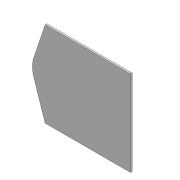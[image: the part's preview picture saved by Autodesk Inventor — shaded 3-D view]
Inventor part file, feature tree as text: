
AUTODESK INVENTOR PART (.ipt)
format: ipt  version: 2018 (Build 220112000, 112)  size: 165,888 bytes
history: native  units: mm
features: projected_geometry x8, sketch x6, extrude x4, fillet x2, hole x2
ambient origin geometry x8: Origin, YZ Plane, XZ Plane, XY Plane, X Axis, Y Axis, Z Axis, Center Point
bodies: Solid1 (feature_tree)
feature tree (22):
  extrude  "Extrusion1"  Depth=30.0mm
  extrude  "Extrusion2"  Depth=150.0mm
  extrude  "Extrusion3"  Depth=150.0mm TaperAngle=0.0deg
  extrude  "Extrusion4"  Depth=15.0mm TaperAngle=0.0deg
  fillet  "Fillet1"  Radius=12.5mm
  hole  "Hole1"  [1 undecoded]
  fillet  "Fillet2"  Radius=5.0mm
  hole  "Hole2"  [1 undecoded]
  sketch  "Sketch1"  dims[d0=100.0mm d1=30.0mm]
  sketch  "Sketch2"  dims[d2=30.0mm d3=0.0mm d4=150.0mm]
  projected_geometry  "Projected Loop1"
  sketch  "Sketch3"  dims[d5=150.0mm d6=3.0mm d7=0.0mm]
  projected_geometry  "Projected Loop2"
  sketch  "Sketch4"  dims[d8=40.0mm d9=15.0mm d10=0.0mm d11=12.5mm]
  projected_geometry  "Projected Loop3"
  sketch  "Sketch5"  dims[d12=21.0mm d13=8.0mm d14=5.0mm]
  projected_geometry  "Projected Loop4"
  sketch  "Sketch6"  dims[d15=5.0mm d16=5.0mm d17=5.0mm d18=5.0mm d19=7.0mm d20=0.0mm d21=2.0mm d22=20.0mm d23=4.5mm d24=6.0mm d25=8.0mm d26=55.0mm d27=90.0deg d28=8.0mm d29=20.594885mm d30=1.0mm d31=1.567mm d32=10.0mm d33=8.0mm d34=55.0mm d35=90.0deg d36=10.0mm d37=20.594885mm]
  projected_geometry  "Projected Loop5"
  projected_geometry  "Projected Loop6"
  projected_geometry  "Projected Loop7"
  projected_geometry  "Projected Loop8"
note: 2 required parameter values undecoded (feature->parameter linkage not recoverable at this tier; creation-order binding heuristic only, values carry confidence <= 0.55)
